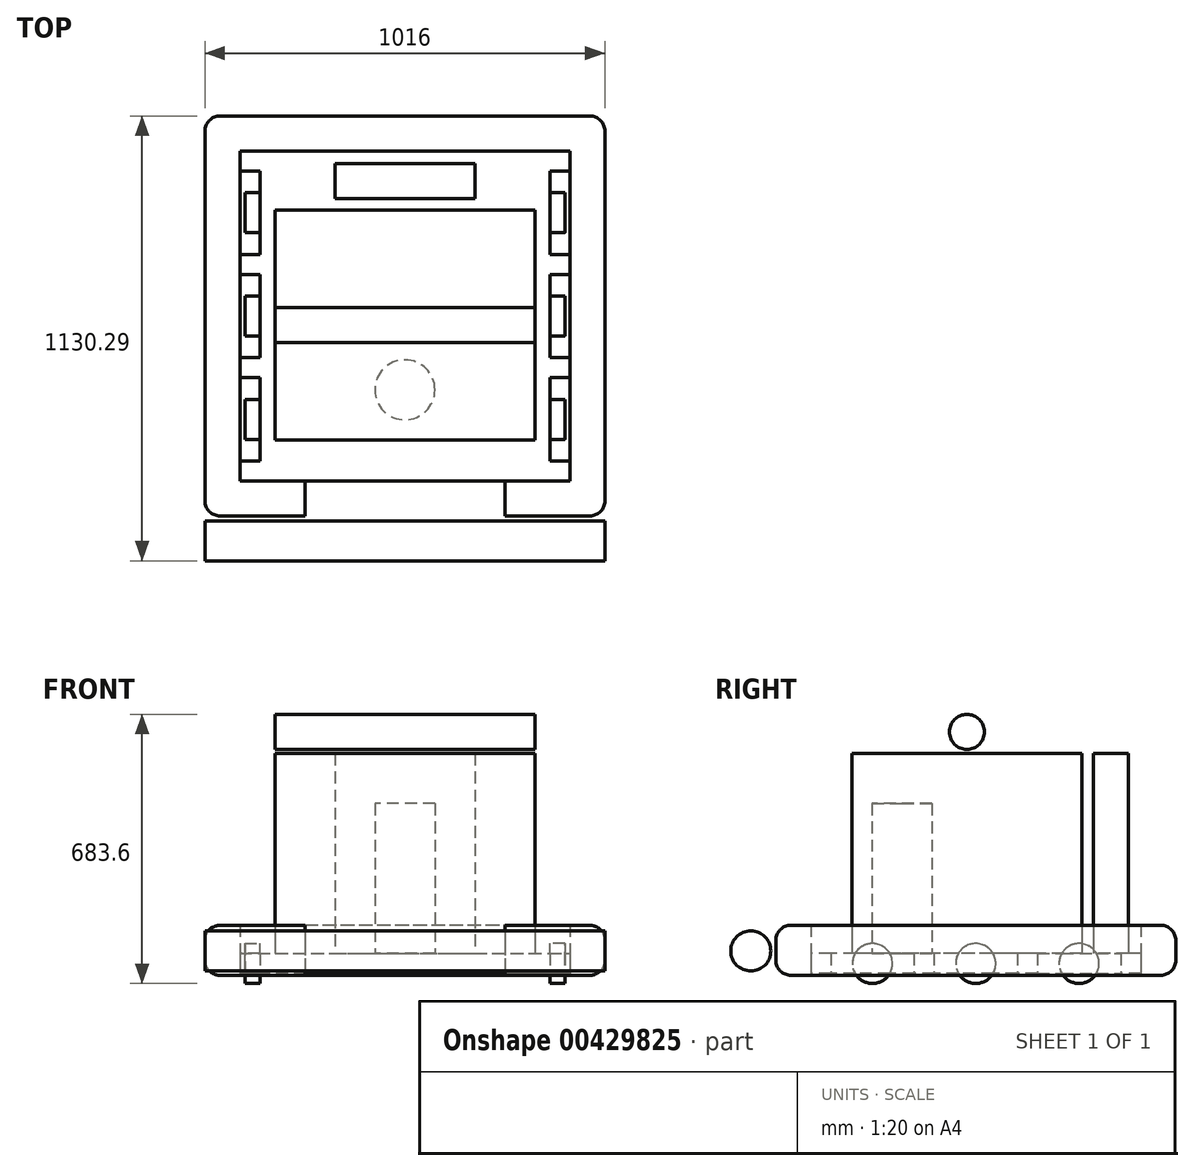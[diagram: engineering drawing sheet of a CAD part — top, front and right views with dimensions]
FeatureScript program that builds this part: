
annotation { "Feature Type Name" : "Feature", "Feature Type Description" : "" }
export const myFeature = defineFeature(function(context is Context, id is Id, definition is map)
    precondition{}
    {
        {
            var Q0;
            Q0=qCreatedBy(makeId("Top.planeOp"),FACE);
            var sketch = newSketch(context, id + "F0", { "sketchPlane" : qUnion([Q0])});
            skLineSegment(sketch, "E0.bottom", {"start": v(-466.7, 636.85) * mm, "end": v(371.5, 636.85) * mm});
            skLineSegment(sketch, "E0.top", {"start": v(-466.7, -201.35) * mm, "end": v(371.5, -201.35) * mm});
            skLineSegment(sketch, "E0.left", {"start": v(-466.7, 636.85) * mm, "end": v(-466.7, 586.05) * mm});
            skLineSegment(sketch, "E0.right", {"start": v(371.5, 636.85) * mm, "end": v(371.5, 586.05) * mm});
            skPoint(sketch, "E0.middle", {"position": v(-47.6, 217.75) * mm});
            skLineSegment(sketch, "E1", {"start": v(-47.6, 636.85) * mm, "end": v(-47.6, -201.35) * mm, "construction": true});
            skLineSegment(sketch, "E2", {"start": v(-466.7, 374.38) * mm, "end": v(-415.9, 374.38) * mm});
            skLineSegment(sketch, "E3", {"start": v(-415.9, 374.38) * mm, "end": v(-415.9, 586.05) * mm});
            skLineSegment(sketch, "E4", {"start": v(-415.9, 586.05) * mm, "end": v(-466.7, 586.05) * mm});
            skLineSegment(sketch, "E5", {"start": v(-466.7, 323.58) * mm, "end": v(-415.9, 323.58) * mm});
            skLineSegment(sketch, "E6", {"start": v(-415.9, 323.58) * mm, "end": v(-415.9, 111.91) * mm});
            skLineSegment(sketch, "E7", {"start": v(-415.9, 111.91) * mm, "end": v(-466.7, 111.91) * mm});
            skLineSegment(sketch, "E8", {"start": v(-466.7, 61.11) * mm, "end": v(-415.9, 61.11) * mm});
            skLineSegment(sketch, "E9", {"start": v(-415.9, 61.11) * mm, "end": v(-415.9, -150.55) * mm});
            skLineSegment(sketch, "E10", {"start": v(-415.9, -150.55) * mm, "end": v(-466.7, -150.55) * mm});
            skLineSegment(sketch, "E11", {"start": v(-415.9, 636.85) * mm, "end": v(-415.9, -201.35) * mm, "construction": true});
            skPoint(sketch, "E12", {"position": v(-415.9, 217.75) * mm});
            skLineSegment(sketch, "E13.trimOffspring", {"start": v(-466.7, -150.55) * mm, "end": v(-466.7, -201.35) * mm});
            skLineSegment(sketch, "E14.trimOffspring", {"start": v(-466.7, 111.91) * mm, "end": v(-466.7, 61.11) * mm});
            skLineSegment(sketch, "E15.trimOffspring", {"start": v(-466.7, 374.38) * mm, "end": v(-466.7, 323.58) * mm});
            skLineSegment(sketch, "E16", {"start": v(-466.7, 323.58) * mm, "end": v(-466.7, 111.91) * mm, "construction": true});
            skLineSegment(sketch, "E17", {"start": v(-466.7, 586.05) * mm, "end": v(-466.7, 374.38) * mm, "construction": true});
            skLineSegment(sketch, "E18", {"start": v(-466.7, 61.11) * mm, "end": v(-466.7, -150.55) * mm, "construction": true});
            skLineSegment(sketch, "E19", {"start": v(-441.3, -150.55) * mm, "end": v(-441.3, -201.35) * mm, "construction": true});
            skLineSegment(sketch, "E20", {"start": v(-441.3, 636.85) * mm, "end": v(-441.3, 586.05) * mm, "construction": true});
            skPoint(sketch, "E20.startSnap0", {"position": v(-441.3, 374.38) * mm});
            skLineSegment(sketch, "E21.MirrorCS", {"start": v(320.7, 374.38) * mm, "end": v(320.7, 586.05) * mm});
            skLineSegment(sketch, "E22.MirrorCS", {"start": v(371.5, 374.38) * mm, "end": v(320.7, 374.38) * mm});
            skLineSegment(sketch, "E23.MirrorCS", {"start": v(320.7, 586.05) * mm, "end": v(371.5, 586.05) * mm});
            skLineSegment(sketch, "E24.MirrorCS", {"start": v(320.7, 61.11) * mm, "end": v(320.7, -150.55) * mm});
            skLineSegment(sketch, "E25.MirrorCS", {"start": v(320.7, -150.55) * mm, "end": v(371.5, -150.55) * mm});
            skLineSegment(sketch, "E26.MirrorCS", {"start": v(371.5, 61.11) * mm, "end": v(320.7, 61.11) * mm});
            skLineSegment(sketch, "E27.MirrorCS", {"start": v(320.7, 111.91) * mm, "end": v(371.5, 111.91) * mm});
            skLineSegment(sketch, "E28.MirrorCS", {"start": v(320.7, 323.58) * mm, "end": v(320.7, 111.91) * mm});
            skLineSegment(sketch, "E29.MirrorCS", {"start": v(371.5, 323.58) * mm, "end": v(320.7, 323.58) * mm});
            skLineSegment(sketch, "E30.trimOffspring", {"start": v(371.5, 374.38) * mm, "end": v(371.5, 323.58) * mm});
            skLineSegment(sketch, "E31.trimOffspring", {"start": v(371.5, 111.91) * mm, "end": v(371.5, 61.11) * mm});
            skLineSegment(sketch, "E32.trimOffspring", {"start": v(371.5, -150.55) * mm, "end": v(371.5, -201.35) * mm});
            skSolve(sketch);
        }
        {
            var Q0;
            Q0 = qSketchRegion(id + "F0", true);
            extrude(context, id + "F1", {"entities" : qUnion([Q0]), "depth" : 50.8 * mm});
        }
        {
            var Q0;
            Q0=makeQuery(id+"F1.opExtrude","SWEPT_FACE",FACE,{"disambiguationData":[OSD([sQuery(id+"F0.wireOp",EDGE,"E3")])]});
            var sketch = newSketch(context, id + "F2", { "sketchPlane" : qUnion([Q0])});
            skLineSegment(sketch, "E33.0.0", {"start": v(-586.05, 0) * mm, "end": v(-374.38, 0) * mm});
            skLineSegment(sketch, "E33.0.1", {"start": v(-374.38, 0) * mm, "end": v(-374.38, 50.8) * mm});
            skLineSegment(sketch, "E33.0.2", {"start": v(-374.38, 50.8) * mm, "end": v(-586.05, 50.8) * mm});
            skLineSegment(sketch, "E33.0.3", {"start": v(-586.05, 50.8) * mm, "end": v(-586.05, 0) * mm});
            skLineSegment(sketch, "E34.0.0", {"start": v(-323.58, 0) * mm, "end": v(-111.91, 0) * mm});
            skLineSegment(sketch, "E34.0.1", {"start": v(-111.91, 0) * mm, "end": v(-111.91, 50.8) * mm});
            skLineSegment(sketch, "E34.0.2", {"start": v(-111.91, 50.8) * mm, "end": v(-323.58, 50.8) * mm});
            skLineSegment(sketch, "E34.0.3", {"start": v(-323.58, 50.8) * mm, "end": v(-323.58, 0) * mm});
            skLineSegment(sketch, "E35.0.0", {"start": v(-61.11, 0) * mm, "end": v(150.55, 0) * mm});
            skLineSegment(sketch, "E35.0.1", {"start": v(150.55, 0) * mm, "end": v(150.55, 50.8) * mm});
            skLineSegment(sketch, "E35.0.2", {"start": v(150.55, 50.8) * mm, "end": v(-61.11, 50.8) * mm});
            skLineSegment(sketch, "E35.0.3", {"start": v(-61.11, 50.8) * mm, "end": v(-61.11, 0) * mm});
            skCircle(sketch, "E36", {"center": v(-480.21, 25.4) * mm, "radius": 50.8 * mm});
            skPoint(sketch, "E36.centerSnap0", {"position": v(-586.05, 25.4) * mm});
            skPoint(sketch, "E36.centerSnap1", {"position": v(-480.21, 0) * mm});
            skCircle(sketch, "E37", {"center": v(-217.75, 25.4) * mm, "radius": 50.8 * mm});
            skPoint(sketch, "E37.centerSnap0", {"position": v(-323.58, 25.4) * mm});
            skPoint(sketch, "E37.centerSnap1", {"position": v(-217.75, 50.8) * mm});
            skCircle(sketch, "E38", {"center": v(44.72, 25.4) * mm, "radius": 50.8 * mm});
            skPoint(sketch, "E38.centerSnap0", {"position": v(44.72, 50.8) * mm});
            skPoint(sketch, "E38.centerSnap1", {"position": v(-61.11, 25.4) * mm});
            skSolve(sketch);
        }
        {
            var Q0;
            {var subQ0=sQuery(id+"F2.wireOp",EDGE,"E37");var subQ1=sQuery(id+"F2.wireOp",EDGE,"E34.0.2");var subQ2=makeQuery(id+"F2.imprint","INTERSECT",VERTEX,{"disambiguationData":[OD(0.0)],"derivedFrom":[subQ1,subQ0]});Q0=makeQuery(id+"F2.imprint","IMPRINT",FACE,{"disambiguationData":[TD([[makeQuery(id+"F2.imprint","IMPRINT",EDGE,{"disambiguationData":[TD([[subQ2,-1.0]])],"derivedFrom":subQ1}),-1.0]])]});}
            var Q1;
            {var subQ0=sQuery(id+"F2.wireOp",EDGE,"E37");var subQ1=sQuery(id+"F2.wireOp",EDGE,"E34.0.0");var subQ2=makeQuery(id+"F2.imprint","INTERSECT",VERTEX,{"disambiguationData":[OD(0.0)],"derivedFrom":[subQ1,subQ0]});Q1=makeQuery(id+"F2.imprint","IMPRINT",FACE,{"disambiguationData":[TD([[makeQuery(id+"F2.imprint","IMPRINT",EDGE,{"disambiguationData":[TD([[subQ2,-1.0]])],"derivedFrom":subQ1}),1.0]])]});}
            var Q2;
            {var subQ0=sQuery(id+"F2.wireOp",EDGE,"E37");var subQ1=sQuery(id+"F2.wireOp",EDGE,"E34.0.0");var subQ2=makeQuery(id+"F2.imprint","INTERSECT",VERTEX,{"disambiguationData":[OD(0.0)],"derivedFrom":[subQ1,subQ0]});Q2=makeQuery(id+"F2.imprint","IMPRINT",FACE,{"disambiguationData":[TD([[makeQuery(id+"F2.imprint","IMPRINT",EDGE,{"disambiguationData":[TD([[subQ2,-1.0]])],"derivedFrom":subQ1}),-1.0]])]});}
            var Q3;
            {var subQ0=sQuery(id+"F2.wireOp",EDGE,"E38");var subQ1=sQuery(id+"F2.wireOp",EDGE,"E35.0.2");var subQ2=makeQuery(id+"F2.imprint","INTERSECT",VERTEX,{"disambiguationData":[OD(0.0)],"derivedFrom":[subQ1,subQ0]});Q3=makeQuery(id+"F2.imprint","IMPRINT",FACE,{"disambiguationData":[TD([[makeQuery(id+"F2.imprint","IMPRINT",EDGE,{"disambiguationData":[TD([[subQ2,-1.0]])],"derivedFrom":subQ1}),-1.0]])]});}
            var Q4;
            {var subQ0=sQuery(id+"F2.wireOp",EDGE,"E38");var subQ1=sQuery(id+"F2.wireOp",EDGE,"E35.0.0");var subQ2=makeQuery(id+"F2.imprint","INTERSECT",VERTEX,{"disambiguationData":[OD(0.0)],"derivedFrom":[subQ1,subQ0]});Q4=makeQuery(id+"F2.imprint","IMPRINT",FACE,{"disambiguationData":[TD([[makeQuery(id+"F2.imprint","IMPRINT",EDGE,{"disambiguationData":[TD([[subQ2,-1.0]])],"derivedFrom":subQ1}),1.0]])]});}
            var Q5;
            {var subQ0=sQuery(id+"F2.wireOp",EDGE,"E38");var subQ1=sQuery(id+"F2.wireOp",EDGE,"E35.0.0");var subQ2=makeQuery(id+"F2.imprint","INTERSECT",VERTEX,{"disambiguationData":[OD(0.0)],"derivedFrom":[subQ1,subQ0]});Q5=makeQuery(id+"F2.imprint","IMPRINT",FACE,{"disambiguationData":[TD([[makeQuery(id+"F2.imprint","IMPRINT",EDGE,{"disambiguationData":[TD([[subQ2,-1.0]])],"derivedFrom":subQ1}),-1.0]])]});}
            var Q6;
            {var subQ0=sQuery(id+"F2.wireOp",EDGE,"E36");var subQ1=sQuery(id+"F2.wireOp",EDGE,"E33.0.2");var subQ2=makeQuery(id+"F2.imprint","INTERSECT",VERTEX,{"disambiguationData":[OD(0.0)],"derivedFrom":[subQ1,subQ0]});Q6=makeQuery(id+"F2.imprint","IMPRINT",FACE,{"disambiguationData":[TD([[makeQuery(id+"F2.imprint","IMPRINT",EDGE,{"disambiguationData":[TD([[subQ2,-1.0]])],"derivedFrom":subQ1}),-1.0]])]});}
            var Q7;
            {var subQ0=sQuery(id+"F2.wireOp",EDGE,"E36");var subQ1=sQuery(id+"F2.wireOp",EDGE,"E33.0.0");var subQ2=makeQuery(id+"F2.imprint","INTERSECT",VERTEX,{"disambiguationData":[OD(0.0)],"derivedFrom":[subQ1,subQ0]});Q7=makeQuery(id+"F2.imprint","IMPRINT",FACE,{"disambiguationData":[TD([[makeQuery(id+"F2.imprint","IMPRINT",EDGE,{"disambiguationData":[TD([[subQ2,-1.0]])],"derivedFrom":subQ1}),-1.0]])]});}
            var Q8;
            {var subQ0=sQuery(id+"F2.wireOp",EDGE,"E36");var subQ1=sQuery(id+"F2.wireOp",EDGE,"E33.0.0");var subQ2=makeQuery(id+"F2.imprint","INTERSECT",VERTEX,{"disambiguationData":[OD(0.0)],"derivedFrom":[subQ1,subQ0]});Q8=makeQuery(id+"F2.imprint","IMPRINT",FACE,{"disambiguationData":[TD([[makeQuery(id+"F2.imprint","IMPRINT",EDGE,{"disambiguationData":[TD([[subQ2,-1.0]])],"derivedFrom":subQ1}),1.0]])]});}
            extrude(context, id + "F3", {"entities" : qUnion([Q0, Q1, Q2, Q3, Q4, Q5, Q6, Q7, Q8]), "operationType" : NewBodyOperationType.ADD, "depth" : 38.1 * mm});
        }
        {
            var Q0;
            Q0=makeQuery(id+"F1.opExtrude","SWEPT_FACE",FACE,{"disambiguationData":[OSD([sQuery(id+"F0.wireOp",EDGE,"E24.MirrorCS")])]});
            var sketch = newSketch(context, id + "F4", { "sketchPlane" : qUnion([Q0])});
            skLineSegment(sketch, "E39.0.0", {"start": v(-150.55, 0) * mm, "end": v(61.11, 0) * mm});
            skLineSegment(sketch, "E39.0.1", {"start": v(61.11, 0) * mm, "end": v(61.11, 50.8) * mm});
            skLineSegment(sketch, "E39.0.2", {"start": v(61.11, 50.8) * mm, "end": v(-150.55, 50.8) * mm});
            skLineSegment(sketch, "E39.0.3", {"start": v(-150.55, 50.8) * mm, "end": v(-150.55, 0) * mm});
            skLineSegment(sketch, "E40.0.0", {"start": v(111.91, 0) * mm, "end": v(323.58, 0) * mm});
            skLineSegment(sketch, "E40.0.1", {"start": v(323.58, 0) * mm, "end": v(323.58, 50.8) * mm});
            skLineSegment(sketch, "E40.0.2", {"start": v(323.58, 50.8) * mm, "end": v(111.91, 50.8) * mm});
            skLineSegment(sketch, "E40.0.3", {"start": v(111.91, 50.8) * mm, "end": v(111.91, 0) * mm});
            skLineSegment(sketch, "E41.0.0", {"start": v(374.38, 0) * mm, "end": v(586.05, 0) * mm});
            skLineSegment(sketch, "E41.0.1", {"start": v(586.05, 0) * mm, "end": v(586.05, 50.8) * mm});
            skLineSegment(sketch, "E41.0.2", {"start": v(586.05, 50.8) * mm, "end": v(374.38, 50.8) * mm});
            skLineSegment(sketch, "E41.0.3", {"start": v(374.38, 50.8) * mm, "end": v(374.38, 0) * mm});
            skCircle(sketch, "E42", {"center": v(-44.72, 25.4) * mm, "radius": 50.8 * mm});
            skPoint(sketch, "E42.centerSnap0", {"position": v(-150.55, 25.4) * mm});
            skPoint(sketch, "E42.centerSnap1", {"position": v(-44.72, 50.8) * mm});
            skCircle(sketch, "E43", {"center": v(217.75, 25.4) * mm, "radius": 50.8 * mm});
            skPoint(sketch, "E43.centerSnap0", {"position": v(111.91, 25.4) * mm});
            skPoint(sketch, "E43.centerSnap1", {"position": v(217.75, 50.8) * mm});
            skCircle(sketch, "E44", {"center": v(480.21, 25.4) * mm, "radius": 50.8 * mm});
            skPoint(sketch, "E44.centerSnap0", {"position": v(480.21, 50.8) * mm});
            skPoint(sketch, "E44.centerSnap1", {"position": v(374.38, 25.4) * mm});
            skSolve(sketch);
        }
        {
            var Q0;
            {var subQ0=sQuery(id+"F4.wireOp",EDGE,"E42");var subQ1=sQuery(id+"F4.wireOp",EDGE,"E39.0.2");var subQ2=makeQuery(id+"F4.imprint","INTERSECT",VERTEX,{"disambiguationData":[OD(0.0)],"derivedFrom":[subQ1,subQ0]});Q0=makeQuery(id+"F4.imprint","IMPRINT",FACE,{"disambiguationData":[TD([[makeQuery(id+"F4.imprint","IMPRINT",EDGE,{"disambiguationData":[TD([[subQ2,-1.0]])],"derivedFrom":subQ1}),-1.0]])]});}
            var Q1;
            {var subQ0=sQuery(id+"F4.wireOp",EDGE,"E42");var subQ1=sQuery(id+"F4.wireOp",EDGE,"E39.0.0");var subQ2=makeQuery(id+"F4.imprint","INTERSECT",VERTEX,{"disambiguationData":[OD(0.0)],"derivedFrom":[subQ1,subQ0]});Q1=makeQuery(id+"F4.imprint","IMPRINT",FACE,{"disambiguationData":[TD([[makeQuery(id+"F4.imprint","IMPRINT",EDGE,{"disambiguationData":[TD([[subQ2,-1.0]])],"derivedFrom":subQ1}),-1.0]])]});}
            var Q2;
            {var subQ0=sQuery(id+"F4.wireOp",EDGE,"E42");var subQ1=sQuery(id+"F4.wireOp",EDGE,"E39.0.0");var subQ2=makeQuery(id+"F4.imprint","INTERSECT",VERTEX,{"disambiguationData":[OD(0.0)],"derivedFrom":[subQ1,subQ0]});Q2=makeQuery(id+"F4.imprint","IMPRINT",FACE,{"disambiguationData":[TD([[makeQuery(id+"F4.imprint","IMPRINT",EDGE,{"disambiguationData":[TD([[subQ2,-1.0]])],"derivedFrom":subQ1}),1.0]])]});}
            var Q3;
            {var subQ0=sQuery(id+"F4.wireOp",EDGE,"E43");var subQ1=sQuery(id+"F4.wireOp",EDGE,"E40.0.2");var subQ2=makeQuery(id+"F4.imprint","INTERSECT",VERTEX,{"disambiguationData":[OD(0.0)],"derivedFrom":[subQ1,subQ0]});Q3=makeQuery(id+"F4.imprint","IMPRINT",FACE,{"disambiguationData":[TD([[makeQuery(id+"F4.imprint","IMPRINT",EDGE,{"disambiguationData":[TD([[subQ2,-1.0]])],"derivedFrom":subQ1}),-1.0]])]});}
            var Q4;
            {var subQ0=sQuery(id+"F4.wireOp",EDGE,"E43");var subQ1=sQuery(id+"F4.wireOp",EDGE,"E40.0.0");var subQ2=makeQuery(id+"F4.imprint","INTERSECT",VERTEX,{"disambiguationData":[OD(0.0)],"derivedFrom":[subQ1,subQ0]});Q4=makeQuery(id+"F4.imprint","IMPRINT",FACE,{"disambiguationData":[TD([[makeQuery(id+"F4.imprint","IMPRINT",EDGE,{"disambiguationData":[TD([[subQ2,-1.0]])],"derivedFrom":subQ1}),1.0]])]});}
            var Q5;
            {var subQ0=sQuery(id+"F4.wireOp",EDGE,"E43");var subQ1=sQuery(id+"F4.wireOp",EDGE,"E40.0.0");var subQ2=makeQuery(id+"F4.imprint","INTERSECT",VERTEX,{"disambiguationData":[OD(0.0)],"derivedFrom":[subQ1,subQ0]});Q5=makeQuery(id+"F4.imprint","IMPRINT",FACE,{"disambiguationData":[TD([[makeQuery(id+"F4.imprint","IMPRINT",EDGE,{"disambiguationData":[TD([[subQ2,-1.0]])],"derivedFrom":subQ1}),-1.0]])]});}
            var Q6;
            {var subQ0=sQuery(id+"F4.wireOp",EDGE,"E44");var subQ1=sQuery(id+"F4.wireOp",EDGE,"E41.0.2");var subQ2=makeQuery(id+"F4.imprint","INTERSECT",VERTEX,{"disambiguationData":[OD(0.0)],"derivedFrom":[subQ1,subQ0]});Q6=makeQuery(id+"F4.imprint","IMPRINT",FACE,{"disambiguationData":[TD([[makeQuery(id+"F4.imprint","IMPRINT",EDGE,{"disambiguationData":[TD([[subQ2,-1.0]])],"derivedFrom":subQ1}),-1.0]])]});}
            var Q7;
            {var subQ0=sQuery(id+"F4.wireOp",EDGE,"E44");var subQ1=sQuery(id+"F4.wireOp",EDGE,"E41.0.0");var subQ2=makeQuery(id+"F4.imprint","INTERSECT",VERTEX,{"disambiguationData":[OD(0.0)],"derivedFrom":[subQ1,subQ0]});Q7=makeQuery(id+"F4.imprint","IMPRINT",FACE,{"disambiguationData":[TD([[makeQuery(id+"F4.imprint","IMPRINT",EDGE,{"disambiguationData":[TD([[subQ2,-1.0]])],"derivedFrom":subQ1}),1.0]])]});}
            var Q8;
            {var subQ0=sQuery(id+"F4.wireOp",EDGE,"E44");var subQ1=sQuery(id+"F4.wireOp",EDGE,"E41.0.0");var subQ2=makeQuery(id+"F4.imprint","INTERSECT",VERTEX,{"disambiguationData":[OD(0.0)],"derivedFrom":[subQ1,subQ0]});Q8=makeQuery(id+"F4.imprint","IMPRINT",FACE,{"disambiguationData":[TD([[makeQuery(id+"F4.imprint","IMPRINT",EDGE,{"disambiguationData":[TD([[subQ2,-1.0]])],"derivedFrom":subQ1}),-1.0]])]});}
            extrude(context, id + "F5", {"entities" : qUnion([Q0, Q1, Q2, Q3, Q4, Q5, Q6, Q7, Q8]), "operationType" : NewBodyOperationType.ADD, "depth" : 38.1 * mm});
        }
        {
            var Q0;
            Q0=makeQuery(id+"F1.opExtrude","CAP_FACE",FACE,{"disambiguationData":[OSD([sQuery(id+"F0.wireOp",EDGE,"E0.bottom"),sQuery(id+"F0.wireOp",EDGE,"E0.top"),sQuery(id+"F0.wireOp",EDGE,"E0.left"),sQuery(id+"F0.wireOp",EDGE,"E0.right"),sQuery(id+"F0.wireOp",EDGE,"E2"),sQuery(id+"F0.wireOp",EDGE,"E3"),sQuery(id+"F0.wireOp",EDGE,"E4"),sQuery(id+"F0.wireOp",EDGE,"E5"),sQuery(id+"F0.wireOp",EDGE,"E6"),sQuery(id+"F0.wireOp",EDGE,"E7"),sQuery(id+"F0.wireOp",EDGE,"E8"),sQuery(id+"F0.wireOp",EDGE,"E9"),sQuery(id+"F0.wireOp",EDGE,"E10"),sQuery(id+"F0.wireOp",EDGE,"E13.trimOffspring"),sQuery(id+"F0.wireOp",EDGE,"E14.trimOffspring"),sQuery(id+"F0.wireOp",EDGE,"E15.trimOffspring"),sQuery(id+"F0.wireOp",EDGE,"E21.MirrorCS"),sQuery(id+"F0.wireOp",EDGE,"E22.MirrorCS"),sQuery(id+"F0.wireOp",EDGE,"E23.MirrorCS"),sQuery(id+"F0.wireOp",EDGE,"E24.MirrorCS"),sQuery(id+"F0.wireOp",EDGE,"E25.MirrorCS"),sQuery(id+"F0.wireOp",EDGE,"E26.MirrorCS"),sQuery(id+"F0.wireOp",EDGE,"E27.MirrorCS"),sQuery(id+"F0.wireOp",EDGE,"E28.MirrorCS"),sQuery(id+"F0.wireOp",EDGE,"E29.MirrorCS"),sQuery(id+"F0.wireOp",EDGE,"E30.trimOffspring"),sQuery(id+"F0.wireOp",EDGE,"E31.trimOffspring"),sQuery(id+"F0.wireOp",EDGE,"E32.trimOffspring")])],"isStart":false});
            cPlane(context, id + "F6", {"entities" : qUnion([Q0]), "cplaneType" : CPlaneType.OFFSET, "offset" : 0 * mm, "width" : 152.4 * mm, "height" : 152.4 * mm});
        }
        {
            var Q0;
            Q0=qCreatedBy(id+"F6.planeOp",FACE);
            var sketch = newSketch(context, id + "F7", { "sketchPlane" : qUnion([Q0])});
            skLineSegment(sketch, "E45.0.0", {"start": v(-466.7, 636.85) * mm, "end": v(-466.7, 636.85) * mm});
            skLineSegment(sketch, "E45.0.1", {"start": v(-466.7, -201.35) * mm, "end": v(371.5, -201.35) * mm});
            skLineSegment(sketch, "E45.0.2", {"start": v(371.5, -201.35) * mm, "end": v(371.5, 636.85) * mm});
            skLineSegment(sketch, "E45.0.3", {"start": v(371.5, 636.85) * mm, "end": v(-390.5, 636.85) * mm});
            skPoint(sketch, "E46.middle", {"position": v(-9.5, 260.08) * mm});
            skPoint(sketch, "E46.middle.positionSnap0", {"position": v(-466.7, 260.08) * mm});
            skPoint(sketch, "E46.middle.positionSnap1", {"position": v(-9.5, 636.85) * mm});
            skPoint(sketch, "E46.centerSnap0", {"position": v(-466.7, 260.08) * mm});
            skPoint(sketch, "E46.centerSnap1", {"position": v(-9.5, 636.85) * mm});
            skLineSegment(sketch, "E47.0", {"start": v(-511.15, 681.3) * mm, "end": v(-511.15, -245.8) * mm});
            skLineSegment(sketch, "E47.1", {"start": v(415.95, 681.3) * mm, "end": v(-511.15, 681.3) * mm});
            skLineSegment(sketch, "E47.2", {"start": v(415.95, -245.8) * mm, "end": v(415.95, 681.3) * mm});
            skLineSegment(sketch, "E47.3", {"start": v(-511.15, -245.8) * mm, "end": v(-301.6, -245.8) * mm});
            skLineSegment(sketch, "E48", {"start": v(-301.6, -246.64) * mm, "end": v(206.4, -246.64) * mm, "construction": true});
            skPoint(sketch, "E49", {"position": v(-47.6, -201.35) * mm});
            skPoint(sketch, "E50", {"position": v(-47.6, -246.64) * mm});
            skLineSegment(sketch, "E51", {"start": v(-301.6, -246.64) * mm, "end": v(-301.6, -245.8) * mm, "construction": true});
            skLineSegment(sketch, "E52", {"start": v(206.4, -246.64) * mm, "end": v(206.4, -245.8) * mm, "construction": true});
            skLineSegment(sketch, "E53.trimOffspring", {"start": v(206.4, -245.8) * mm, "end": v(415.95, -245.8) * mm});
            skSolve(sketch);
        }
        {
            var Q0;
            Q0=sQuery(id+"F7.wireOp",EDGE,"E52");
            cPlane(context, id + "F8", {"entities" : qUnion([Q0]), "cplaneType" : CPlaneType.LINE_ANGLE, "offset" : 25.4 * mm, "angle" : 90 * degree, "width" : 152.4 * mm, "height" : 152.4 * mm});
        }
        {
            var Q0;
            Q0=qCreatedBy(id+"F8.planeOp",FACE);
            var sketch = newSketch(context, id + "F9", { "sketchPlane" : qUnion([Q0])});
            skLineSegment(sketch, "E54.0", {"start": v(-201.35, 50.8) * mm, "end": v(-201.35, 0) * mm});
            skLineSegment(sketch, "E55.0", {"start": v(-246.64, 50.8) * mm, "end": v(-245.8, 50.8) * mm});
            skLineSegment(sketch, "E56.bottom", {"start": v(-201.35, 122.33) * mm, "end": v(-252.15, 122.33) * mm});
            skLineSegment(sketch, "E56.top", {"start": v(-201.35, -4.67) * mm, "end": v(-252.15, -4.67) * mm});
            skLineSegment(sketch, "E56.left", {"start": v(-201.35, 122.33) * mm, "end": v(-201.35, -4.67) * mm});
            skLineSegment(sketch, "E56.right", {"start": v(-290.25, 84.23) * mm, "end": v(-290.25, 33.43) * mm});
            skPoint(sketch, "E56.middle", {"position": v(-245.8, 58.83) * mm});
            skPoint(sketch, "E57.visualSharp", {"position": v(-290.25, 122.33) * mm});
            skArc(sketch, "E57.filletArc", {"start": v(-252.15, 122.33) * mm, "mid": v(-279.1, 111.17) * mm, "end": v(-290.25, 84.23) * mm});
            skPoint(sketch, "E58.visualSharp", {"position": v(-290.25, -4.67) * mm});
            skArc(sketch, "E58.filletArc", {"start": v(-290.25, 33.43) * mm, "mid": v(-279.1, 6.49) * mm, "end": v(-252.15, -4.67) * mm});
            skSolve(sketch);
        }
        {
            var Q0;
            {var subQ1=sQuery(id+"F9.wireOp",EDGE,"E56.bottom");Q0=makeQuery(id+"F9.imprint","IMPRINT",FACE,{"disambiguationData":[TD([[makeQuery(id+"F9.imprint","IMPRINT",EDGE,{"derivedFrom":subQ1}),1.0]])]});}
            var Q1;
            Q1=sQuery(id+"F7.wireOp",EDGE,"E53.trimOffspring");
            var Q2;
            Q2=sQuery(id+"F7.wireOp",EDGE,"E47.2");
            var Q3;
            Q3=sQuery(id+"F7.wireOp",EDGE,"E47.1");
            var Q4;
            Q4=sQuery(id+"F7.wireOp",EDGE,"E47.0");
            var Q5;
            Q5=sQuery(id+"F7.wireOp",EDGE,"E47.3");
            sweep(context, id + "F10", {"profiles" : qUnion([Q0]), "path" : qUnion([Q1, Q2, Q3, Q4, Q5])});
        }
        {
            var Q0;
            Q0=makeQuery(id+"F10.opSweep","MID_CAP_EDGE",EDGE,{"disambiguationData":[OSD([sQuery(id+"F7.wireOp",VERTEX,"E47.3.start"),sQuery(id+"F9.wireOp",EDGE,"E56.right")])],"capPos":4.0});
            var Q1;
            Q1=makeQuery(id+"F10.opSweep","MID_CAP_EDGE",EDGE,{"disambiguationData":[OSD([sQuery(id+"F7.wireOp",VERTEX,"E47.2.start"),sQuery(id+"F9.wireOp",EDGE,"E56.right")])],"capPos":1.0});
            var Q2;
            Q2=makeQuery(id+"F10.opSweep","MID_CAP_EDGE",EDGE,{"disambiguationData":[OSD([sQuery(id+"F7.wireOp",VERTEX,"E47.1.start"),sQuery(id+"F9.wireOp",EDGE,"E56.right")])],"capPos":2.0});
            var Q3;
            Q3=makeQuery(id+"F10.opSweep","MID_CAP_EDGE",EDGE,{"disambiguationData":[OSD([sQuery(id+"F7.wireOp",VERTEX,"E47.0.start"),sQuery(id+"F9.wireOp",EDGE,"E56.right")])],"capPos":3.0});
            fillet(context, id + "F11", {"entities" : qUnion([Q0, Q1, Q2, Q3]), "radius" : 38.1 * mm, "tangentPropagation" : true, "allowEdgeOverflow" : false});
        }
        {
            var Q0;
            Q0=makeQuery(id+"F1.opExtrude","CAP_FACE",FACE,{"disambiguationData":[OSD([sQuery(id+"F0.wireOp",EDGE,"E0.bottom"),sQuery(id+"F0.wireOp",EDGE,"E0.top"),sQuery(id+"F0.wireOp",EDGE,"E0.left"),sQuery(id+"F0.wireOp",EDGE,"E0.right"),sQuery(id+"F0.wireOp",EDGE,"E2"),sQuery(id+"F0.wireOp",EDGE,"E3"),sQuery(id+"F0.wireOp",EDGE,"E4"),sQuery(id+"F0.wireOp",EDGE,"E5"),sQuery(id+"F0.wireOp",EDGE,"E6"),sQuery(id+"F0.wireOp",EDGE,"E7"),sQuery(id+"F0.wireOp",EDGE,"E8"),sQuery(id+"F0.wireOp",EDGE,"E9"),sQuery(id+"F0.wireOp",EDGE,"E10"),sQuery(id+"F0.wireOp",EDGE,"E13.trimOffspring"),sQuery(id+"F0.wireOp",EDGE,"E14.trimOffspring"),sQuery(id+"F0.wireOp",EDGE,"E15.trimOffspring"),sQuery(id+"F0.wireOp",EDGE,"E21.MirrorCS"),sQuery(id+"F0.wireOp",EDGE,"E22.MirrorCS"),sQuery(id+"F0.wireOp",EDGE,"E23.MirrorCS"),sQuery(id+"F0.wireOp",EDGE,"E24.MirrorCS"),sQuery(id+"F0.wireOp",EDGE,"E25.MirrorCS"),sQuery(id+"F0.wireOp",EDGE,"E26.MirrorCS"),sQuery(id+"F0.wireOp",EDGE,"E27.MirrorCS"),sQuery(id+"F0.wireOp",EDGE,"E28.MirrorCS"),sQuery(id+"F0.wireOp",EDGE,"E29.MirrorCS"),sQuery(id+"F0.wireOp",EDGE,"E30.trimOffspring"),sQuery(id+"F0.wireOp",EDGE,"E31.trimOffspring"),sQuery(id+"F0.wireOp",EDGE,"E32.trimOffspring")])],"isStart":false});
            var sketch = newSketch(context, id + "F12", { "sketchPlane" : qUnion([Q0])});
            skLineSegment(sketch, "E59.0.0", {"start": v(371.5, -150.55) * mm, "end": v(320.7, -150.55) * mm});
            skLineSegment(sketch, "E59.0.1", {"start": v(320.7, -150.55) * mm, "end": v(320.7, -88.72) * mm});
            skLineSegment(sketch, "E59.0.2", {"start": v(320.7, -88.72) * mm, "end": v(320.7, -0.73) * mm});
            skLineSegment(sketch, "E59.0.3", {"start": v(320.7, -0.73) * mm, "end": v(320.7, 61.11) * mm});
            skLineSegment(sketch, "E59.0.4", {"start": v(320.7, 61.11) * mm, "end": v(371.5, 61.11) * mm});
            skLineSegment(sketch, "E59.0.5", {"start": v(371.5, 61.11) * mm, "end": v(371.5, 111.91) * mm});
            skLineSegment(sketch, "E59.0.6", {"start": v(371.5, 111.91) * mm, "end": v(320.7, 111.91) * mm});
            skLineSegment(sketch, "E59.0.7", {"start": v(320.7, 111.91) * mm, "end": v(320.7, 173.75) * mm});
            skLineSegment(sketch, "E59.0.8", {"start": v(320.7, 173.75) * mm, "end": v(320.7, 261.74) * mm});
            skLineSegment(sketch, "E59.0.9", {"start": v(320.7, 261.74) * mm, "end": v(320.7, 323.58) * mm});
            skLineSegment(sketch, "E59.0.10", {"start": v(320.7, 323.58) * mm, "end": v(371.5, 323.58) * mm});
            skLineSegment(sketch, "E59.0.11", {"start": v(371.5, 323.58) * mm, "end": v(371.5, 374.38) * mm});
            skLineSegment(sketch, "E59.0.12", {"start": v(371.5, 374.38) * mm, "end": v(320.7, 374.38) * mm});
            skLineSegment(sketch, "E59.0.13", {"start": v(320.7, 374.38) * mm, "end": v(320.7, 436.22) * mm});
            skLineSegment(sketch, "E59.0.14", {"start": v(320.7, 436.22) * mm, "end": v(320.7, 524.2) * mm});
            skLineSegment(sketch, "E59.0.15", {"start": v(320.7, 524.2) * mm, "end": v(320.7, 586.05) * mm});
            skLineSegment(sketch, "E59.0.16", {"start": v(320.7, 586.05) * mm, "end": v(371.5, 586.05) * mm});
            skLineSegment(sketch, "E59.0.17", {"start": v(371.5, 586.05) * mm, "end": v(371.5, 636.85) * mm});
            skLineSegment(sketch, "E59.0.18", {"start": v(371.5, 636.85) * mm, "end": v(-466.7, 636.85) * mm});
            skLineSegment(sketch, "E59.0.19", {"start": v(-466.7, 636.85) * mm, "end": v(-466.7, 586.05) * mm});
            skLineSegment(sketch, "E59.0.20", {"start": v(-466.7, 586.05) * mm, "end": v(-415.9, 586.05) * mm});
            skLineSegment(sketch, "E59.0.21", {"start": v(-415.9, 586.05) * mm, "end": v(-415.9, 524.2) * mm});
            skLineSegment(sketch, "E59.0.22", {"start": v(-415.9, 524.2) * mm, "end": v(-415.9, 436.22) * mm});
            skLineSegment(sketch, "E59.0.23", {"start": v(-415.9, 436.22) * mm, "end": v(-415.9, 374.38) * mm});
            skLineSegment(sketch, "E59.0.24", {"start": v(-415.9, 374.38) * mm, "end": v(-466.7, 374.38) * mm});
            skLineSegment(sketch, "E59.0.25", {"start": v(-466.7, 374.38) * mm, "end": v(-466.7, 323.58) * mm});
            skLineSegment(sketch, "E59.0.26", {"start": v(-466.7, 323.58) * mm, "end": v(-415.9, 323.58) * mm});
            skLineSegment(sketch, "E59.0.27", {"start": v(-415.9, 323.58) * mm, "end": v(-415.9, 261.74) * mm});
            skLineSegment(sketch, "E59.0.28", {"start": v(-415.9, 261.74) * mm, "end": v(-415.9, 173.75) * mm});
            skLineSegment(sketch, "E59.0.29", {"start": v(-415.9, 173.75) * mm, "end": v(-415.9, 111.91) * mm});
            skLineSegment(sketch, "E59.0.30", {"start": v(-415.9, 111.91) * mm, "end": v(-466.7, 111.91) * mm});
            skLineSegment(sketch, "E59.0.31", {"start": v(-466.7, 111.91) * mm, "end": v(-466.7, 61.11) * mm});
            skLineSegment(sketch, "E59.0.32", {"start": v(-466.7, 61.11) * mm, "end": v(-415.9, 61.11) * mm});
            skLineSegment(sketch, "E59.0.33", {"start": v(-415.9, 61.11) * mm, "end": v(-415.9, -0.73) * mm});
            skLineSegment(sketch, "E59.0.34", {"start": v(-415.9, -0.73) * mm, "end": v(-415.9, -88.72) * mm});
            skLineSegment(sketch, "E59.0.35", {"start": v(-415.9, -88.72) * mm, "end": v(-415.9, -150.55) * mm});
            skLineSegment(sketch, "E59.0.36", {"start": v(-415.9, -150.55) * mm, "end": v(-466.7, -150.55) * mm});
            skLineSegment(sketch, "E59.0.37", {"start": v(-466.7, -150.55) * mm, "end": v(-466.7, -201.35) * mm});
            skLineSegment(sketch, "E59.0.38", {"start": v(-466.7, -201.35) * mm, "end": v(371.5, -201.35) * mm});
            skLineSegment(sketch, "E59.0.39", {"start": v(371.5, -201.35) * mm, "end": v(371.5, -150.55) * mm});
            skLineSegment(sketch, "E60.bottom", {"start": v(-377.8, 487.34) * mm, "end": v(282.6, 487.34) * mm});
            skLineSegment(sketch, "E60.top", {"start": v(-377.8, -96.86) * mm, "end": v(282.6, -96.86) * mm});
            skLineSegment(sketch, "E60.left", {"start": v(-377.8, 487.34) * mm, "end": v(-377.8, -96.86) * mm});
            skLineSegment(sketch, "E60.right", {"start": v(282.6, 487.34) * mm, "end": v(282.6, -96.86) * mm});
            skPoint(sketch, "E60.middle", {"position": v(-47.6, 195.24) * mm});
            skPoint(sketch, "E60.middle.positionSnap0", {"position": v(-47.6, -201.35) * mm});
            skPoint(sketch, "E60.centerSnap0", {"position": v(-47.6, -201.35) * mm});
            skSolve(sketch);
        }
        {
            var Q0;
            Q0=makeQuery(id+"F12.imprint","IMPRINT",FACE,{"disambiguationData":[TD([[makeQuery(id+"F12.imprint","IMPRINT",EDGE,{"derivedFrom":sQuery(id+"F12.wireOp",EDGE,"E60.bottom")}),-1.0]])]});
            extrude(context, id + "F13", {"entities" : qUnion([Q0]), "depth" : 508 * mm});
        }
        {
            var Q0;
            Q0=makeQuery(id+"F1.opExtrude","CAP_FACE",FACE,{"disambiguationData":[OSD([sQuery(id+"F0.wireOp",EDGE,"E0.bottom"),sQuery(id+"F0.wireOp",EDGE,"E0.top"),sQuery(id+"F0.wireOp",EDGE,"E0.left"),sQuery(id+"F0.wireOp",EDGE,"E0.right"),sQuery(id+"F0.wireOp",EDGE,"E2"),sQuery(id+"F0.wireOp",EDGE,"E3"),sQuery(id+"F0.wireOp",EDGE,"E4"),sQuery(id+"F0.wireOp",EDGE,"E5"),sQuery(id+"F0.wireOp",EDGE,"E6"),sQuery(id+"F0.wireOp",EDGE,"E7"),sQuery(id+"F0.wireOp",EDGE,"E8"),sQuery(id+"F0.wireOp",EDGE,"E9"),sQuery(id+"F0.wireOp",EDGE,"E10"),sQuery(id+"F0.wireOp",EDGE,"E13.trimOffspring"),sQuery(id+"F0.wireOp",EDGE,"E14.trimOffspring"),sQuery(id+"F0.wireOp",EDGE,"E15.trimOffspring"),sQuery(id+"F0.wireOp",EDGE,"E21.MirrorCS"),sQuery(id+"F0.wireOp",EDGE,"E22.MirrorCS"),sQuery(id+"F0.wireOp",EDGE,"E23.MirrorCS"),sQuery(id+"F0.wireOp",EDGE,"E24.MirrorCS"),sQuery(id+"F0.wireOp",EDGE,"E25.MirrorCS"),sQuery(id+"F0.wireOp",EDGE,"E26.MirrorCS"),sQuery(id+"F0.wireOp",EDGE,"E27.MirrorCS"),sQuery(id+"F0.wireOp",EDGE,"E28.MirrorCS"),sQuery(id+"F0.wireOp",EDGE,"E29.MirrorCS"),sQuery(id+"F0.wireOp",EDGE,"E30.trimOffspring"),sQuery(id+"F0.wireOp",EDGE,"E31.trimOffspring"),sQuery(id+"F0.wireOp",EDGE,"E32.trimOffspring")])],"isStart":false});
            var sketch = newSketch(context, id + "F14", { "sketchPlane" : qUnion([Q0])});
            skLineSegment(sketch, "E61.0", {"start": v(-377.8, -96.86) * mm, "end": v(282.6, -96.86) * mm});
            skCircle(sketch, "E62", {"center": v(-47.6, 30.14) * mm, "radius": 76.2 * mm});
            skPoint(sketch, "E62.centerSnap0", {"position": v(-47.6, -96.86) * mm});
            skSolve(sketch);
        }
        {
            var Q0;
            Q0=makeQuery(id+"F14.imprint","IMPRINT",FACE,{"disambiguationData":[TD([[makeQuery(id+"F14.imprint","IMPRINT",EDGE,{"derivedFrom":sQuery(id+"F14.wireOp",EDGE,"E62")}),1.0]])]});
            extrude(context, id + "F15", {"entities" : qUnion([Q0]), "depth" : 381 * mm});
        }
        {
            var Q0;
            Q0=makeQuery(id+"F1.opExtrude","CAP_FACE",FACE,{"disambiguationData":[OSD([sQuery(id+"F0.wireOp",EDGE,"E0.bottom"),sQuery(id+"F0.wireOp",EDGE,"E0.top"),sQuery(id+"F0.wireOp",EDGE,"E0.left"),sQuery(id+"F0.wireOp",EDGE,"E0.right"),sQuery(id+"F0.wireOp",EDGE,"E2"),sQuery(id+"F0.wireOp",EDGE,"E3"),sQuery(id+"F0.wireOp",EDGE,"E4"),sQuery(id+"F0.wireOp",EDGE,"E5"),sQuery(id+"F0.wireOp",EDGE,"E6"),sQuery(id+"F0.wireOp",EDGE,"E7"),sQuery(id+"F0.wireOp",EDGE,"E8"),sQuery(id+"F0.wireOp",EDGE,"E9"),sQuery(id+"F0.wireOp",EDGE,"E10"),sQuery(id+"F0.wireOp",EDGE,"E13.trimOffspring"),sQuery(id+"F0.wireOp",EDGE,"E14.trimOffspring"),sQuery(id+"F0.wireOp",EDGE,"E15.trimOffspring"),sQuery(id+"F0.wireOp",EDGE,"E21.MirrorCS"),sQuery(id+"F0.wireOp",EDGE,"E22.MirrorCS"),sQuery(id+"F0.wireOp",EDGE,"E23.MirrorCS"),sQuery(id+"F0.wireOp",EDGE,"E24.MirrorCS"),sQuery(id+"F0.wireOp",EDGE,"E25.MirrorCS"),sQuery(id+"F0.wireOp",EDGE,"E26.MirrorCS"),sQuery(id+"F0.wireOp",EDGE,"E27.MirrorCS"),sQuery(id+"F0.wireOp",EDGE,"E28.MirrorCS"),sQuery(id+"F0.wireOp",EDGE,"E29.MirrorCS"),sQuery(id+"F0.wireOp",EDGE,"E30.trimOffspring"),sQuery(id+"F0.wireOp",EDGE,"E31.trimOffspring"),sQuery(id+"F0.wireOp",EDGE,"E32.trimOffspring")])],"isStart":false});
            var sketch = newSketch(context, id + "F16", { "sketchPlane" : qUnion([Q0])});
            skLineSegment(sketch, "E63.bottom", {"start": v(-225.4, 605.28) * mm, "end": v(130.2, 605.28) * mm});
            skLineSegment(sketch, "E63.top", {"start": v(-225.4, 516.38) * mm, "end": v(130.2, 516.38) * mm});
            skLineSegment(sketch, "E63.left", {"start": v(-225.4, 605.28) * mm, "end": v(-225.4, 516.38) * mm});
            skLineSegment(sketch, "E63.right", {"start": v(130.2, 605.28) * mm, "end": v(130.2, 516.38) * mm});
            skPoint(sketch, "E64", {"position": v(-47.6, 516.38) * mm});
            skLineSegment(sketch, "E65.0.0", {"start": v(-377.8, 487.34) * mm, "end": v(-377.8, -96.86) * mm});
            skLineSegment(sketch, "E65.0.1", {"start": v(-377.8, -96.86) * mm, "end": v(282.6, -96.86) * mm});
            skLineSegment(sketch, "E65.0.2", {"start": v(282.6, -96.86) * mm, "end": v(282.6, 487.34) * mm});
            skLineSegment(sketch, "E65.0.3", {"start": v(282.6, 487.34) * mm, "end": v(-377.8, 487.34) * mm});
            skPoint(sketch, "E66", {"position": v(-47.6, 487.34) * mm});
            skSolve(sketch);
        }
        {
            var Q0;
            Q0=makeQuery(id+"F16.imprint","IMPRINT",FACE,{"disambiguationData":[TD([[makeQuery(id+"F16.imprint","IMPRINT",EDGE,{"derivedFrom":sQuery(id+"F16.wireOp",EDGE,"E63.bottom")}),-1.0]])]});
            extrude(context, id + "F17", {"entities" : qUnion([Q0]), "depth" : 508 * mm});
        }
        {
            var Q0;
            Q0=makeQuery(id+"F10.opSweep","SWEPT_FACE",FACE,{"disambiguationData":[OSD([sQuery(id+"F7.wireOp",EDGE,"E47.0"),sQuery(id+"F9.wireOp",EDGE,"E56.right")])]});
            cPlane(context, id + "F18", {"entities" : qUnion([Q0]), "cplaneType" : CPlaneType.OFFSET, "offset" : 0 * mm, "width" : 152.4 * mm, "height" : 152.4 * mm});
        }
        {
            var Q0;
            Q0=qCreatedBy(id+"F18.planeOp",FACE);
            var sketch = newSketch(context, id + "F19", { "sketchPlane" : qUnion([Q0])});
            skCircle(sketch, "E67", {"center": v(353.74, 57) * mm, "radius": 50.8 * mm});
            skSolve(sketch);
        }
        {
            var Q0;
            Q0 = qSketchRegion(id + "F19", true);
            var Q1;
            Q1=makeQuery(id+"F10.opSweep","SWEPT_FACE",FACE,{"disambiguationData":[OSD([sQuery(id+"F7.wireOp",EDGE,"E47.2"),sQuery(id+"F9.wireOp",EDGE,"E56.right")])]});
            extrude(context, id + "F20", {"entities" : qUnion([Q0]), "endBound" : BoundingType.UP_TO_SURFACE, "oppositeDirection" : true, "endBoundEntityFace" : qUnion([Q1]), "depth" : 25.4 * mm});
        }
        {
            var Q0;
            Q0=makeQuery(id+"F13.opExtrude","SWEPT_FACE",FACE,{"disambiguationData":[OSD([sQuery(id+"F12.wireOp",EDGE,"E60.left")])]});
            var sketch = newSketch(context, id + "F21", { "sketchPlane" : qUnion([Q0])});
            skLineSegment(sketch, "E68.0", {"start": v(-487.34, 558.8) * mm, "end": v(96.86, 558.8) * mm});
            skCircle(sketch, "E69", {"center": v(-195.24, 613.75) * mm, "radius": 44.45 * mm});
            skPoint(sketch, "E69.centerSnap0", {"position": v(-195.24, 558.8) * mm});
            skSolve(sketch);
        }
        {
            var Q0;
            Q0 = qSketchRegion(id + "F21", true);
            var Q1;
            Q1=makeQuery(id+"F13.opExtrude","SWEPT_FACE",FACE,{"disambiguationData":[OSD([sQuery(id+"F12.wireOp",EDGE,"E60.right")])]});
            extrude(context, id + "F22", {"entities" : qUnion([Q0]), "endBound" : BoundingType.UP_TO_SURFACE, "oppositeDirection" : true, "endBoundEntityFace" : qUnion([Q1]), "depth" : 25.4 * mm});
        }
    });
